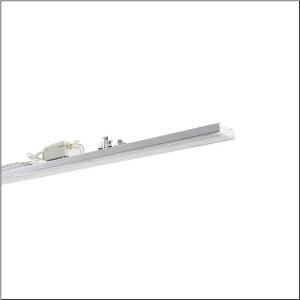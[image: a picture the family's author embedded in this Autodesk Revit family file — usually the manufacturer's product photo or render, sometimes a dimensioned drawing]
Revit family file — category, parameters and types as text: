
# Revit family: licross_21_recessed_ho_52te1emn4e5s
name_source: partatom
category: Lighting Fixtures
units: mm (PartAtom-declared; Revit-internal decimal feet)

## family parameters
Cut with Voids When Loaded = No
Host = Face
Light Source = No
Part Type = Normal
Room Calculation Point = No
Round Connector Dimension = Use Diameter
Shared = No

## types (1)
- --- (1 x LED, 14710 lm, 83.1 W, 4000K)
    Apparent Load = 83 VA
    CIE Flux Codes = 85 95 99 100 100
    Color Rendering = 80
    Color Temperature = 4000K
    Default Elevation = 1800 mm
    Description = Licross 21 Recessed HO, luminaire insert, of sheet steel, galvanised, coil coated, white, length: 1.500mm, width: 66mm, height: 67mm, LED rated luminous flux: 14.710lm, light colour: 840, SDCM (Standard Deviation of Colour Matching)MacAdam ≤ 3 SDCM (initial), control gear: ON/OFF Multilumen, with plug, 3-pole, with phase selection, mains connection: 220..240V, AC, 50/60Hz, rated input power: 83W, internal wiring halogen-free, primary light control with lens, of plastic, primary optical cover: cover, of PMMA, light emission: direct distribution, primary light characteristic: symmetric, protection rating (complete): IP54, insulation class (complete): insulation class I (protective earthing), certification: CE, ENEC, VDE, UKCA, protection symbol: D if used in an environment with non-conductive dust loads with corresponding accessories, impact resistance: IK06, permissible ambient temperature for indoor applications: -35..+30°C, corresponds to IFS (International Featured Standards) requirements for safety and quality in the food industry, reducing of maximum allowable ambient temperature of 5°C with ceiling mounting, LABS conformity tested according to VDMA 24364:2018-05, The light source and the operating device comply with the requirements of the Ecodesign Regulation (EU) 2019/2020 and are replaceable in accordance with this regulation, packaging unit: 1 piece
    Height = 58 mm
    Lamp = 1 x LED
    Lamp Light Flux = 14710 lm
    Lamp Power = 83.1 W
    Lamp count = 1
    Length = 1500 mm
    Luminous efficacy = 177 lm/W
    Manufacturer = Siteco
    ModVariant = No
    Model = 52TE1EMN4E5S
    Mounting Place = Ceiling
    Mounting Type = Pendant
    Number of Poles = 1
    OnlyDefault = Yes
    Power Factor = 1
    Product Name = Licross 21 Recessed HO
    Product group = luminaire insert | ceiling pendant
    ProductGroupID = 901
    Protection Class = Protection class I
    Protection Degree = IP 54
    RLX_Detail_Level = 1
    RLX_Emergency_Light_Flux = 0 lm
    RLX_Emergency_Type = 0
    RLX_Emergency_Type_DB = No
    RlxData = <blob elided: 22649 chars, md5=f3be8815>
    Socket = socket
    Standby Power = 0 W
    System Light Flux = 14710 lm
    System Power = 83 W
    Type Comments = factory setting: luminous flux: 100 % | (A | C | E) | 195 mA
    Type Image = l_1296930.jpg
    URL = http://relux.com
    VarID = @adj_107979
    Voltage = 0 V
    Weight = 0.00 kg
    Width = 66 mm

## geometry (parser evidence)
native form markers: Blend x4, Sweep x11
no freeform markers — native parametric forms only
